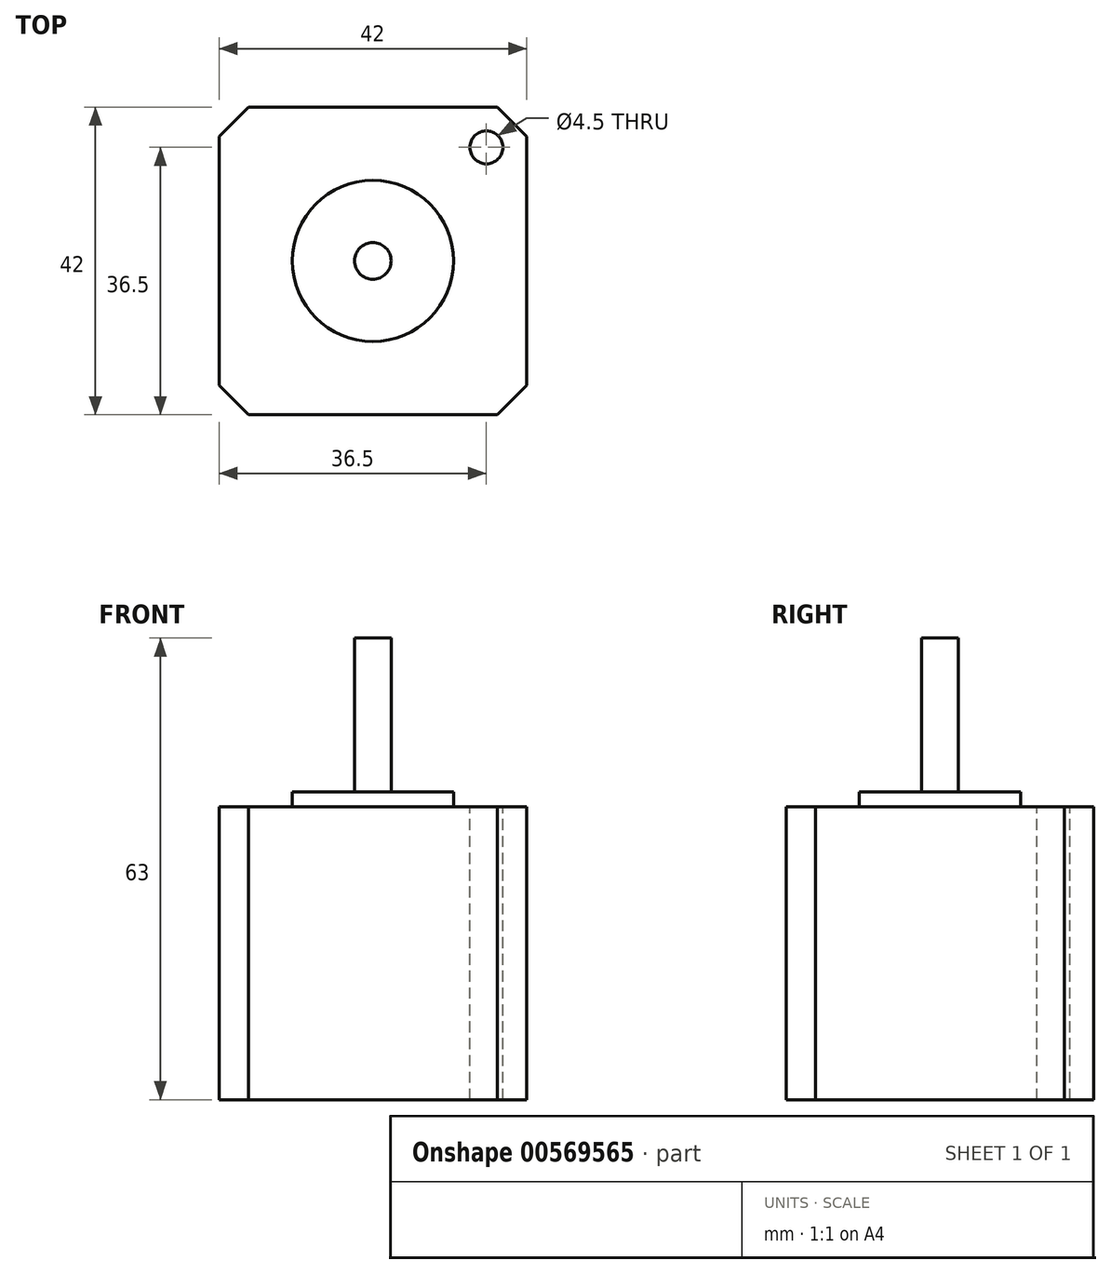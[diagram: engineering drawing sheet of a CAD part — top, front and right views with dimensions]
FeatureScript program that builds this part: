
annotation { "Feature Type Name" : "Feature", "Feature Type Description" : "" }
export const myFeature = defineFeature(function(context is Context, id is Id, definition is map)
    precondition{}
    {
        {
            var Q0;
            Q0=qCreatedBy(makeId("Front.planeOp"),FACE);
            var sketch = newSketch(context, id + "F0", { "sketchPlane" : qUnion([Q0])});
            skLineSegment(sketch, "E0", {"start": v(0, 0) * mm, "end": v(0, 73.77) * mm});
            skSolve(sketch);
        }
        {
            var Q0;
            Q0=qCreatedBy(makeId("Top.planeOp"),FACE);
            var sketch = newSketch(context, id + "F1", { "sketchPlane" : qUnion([Q0])});
            skLineSegment(sketch, "E1.bottom", {"start": v(21, 21) * mm, "end": v(-21, 21) * mm});
            skLineSegment(sketch, "E1.top", {"start": v(21, -21) * mm, "end": v(-21, -21) * mm});
            skLineSegment(sketch, "E1.left", {"start": v(21, 21) * mm, "end": v(21, -21) * mm});
            skLineSegment(sketch, "E1.right", {"start": v(-21, 21) * mm, "end": v(-21, -21) * mm});
            skPoint(sketch, "E1.middle", {"position": v(0, 0) * mm});
            skSolve(sketch);
        }
        {
            var Q0;
            Q0=makeQuery(id+"F1.imprint","IMPRINT",FACE,{"disambiguationData":[TD([[makeQuery(id+"F1.imprint","IMPRINT",EDGE,{"derivedFrom":sQuery(id+"F1.wireOp",EDGE,"E1.bottom")}),1.0]])]});
            extrude(context, id + "F2", {"entities" : qUnion([Q0]), "depth" : 40 * mm, "offsetDistance" : 25 * mm});
        }
        {
            var Q0;
            Q0=makeQuery(id+"F2.opExtrude","CAP_FACE",FACE,{"disambiguationData":[OSD([sQuery(id+"F1.wireOp",EDGE,"E1.bottom"),sQuery(id+"F1.wireOp",EDGE,"E1.top"),sQuery(id+"F1.wireOp",EDGE,"E1.left"),sQuery(id+"F1.wireOp",EDGE,"E1.right")])],"isStart":false});
            var sketch = newSketch(context, id + "F3", { "sketchPlane" : qUnion([Q0])});
            skCircle(sketch, "E2", {"center": v(0, 0) * mm, "radius": 11 * mm});
            skSolve(sketch);
        }
        {
            var Q0;
            Q0 = qSketchRegion(id + "F3", true);
            extrude(context, id + "F4", {"entities" : qUnion([Q0]), "operationType" : NewBodyOperationType.ADD, "depth" : 2 * mm, "offsetDistance" : 25 * mm});
        }
        {
            var Q0;
            Q0=makeQuery(id+"F4.opExtrude","CAP_FACE",FACE,{"disambiguationData":[OSD([sQuery(id+"F3.wireOp",EDGE,"E2")])],"isStart":false});
            var sketch = newSketch(context, id + "F5", { "sketchPlane" : qUnion([Q0])});
            skCircle(sketch, "E3", {"center": v(0, 0) * mm, "radius": 2.5 * mm});
            skSolve(sketch);
        }
        {
            var Q0;
            Q0 = qSketchRegion(id + "F5", true);
            extrude(context, id + "F6", {"entities" : qUnion([Q0]), "operationType" : NewBodyOperationType.ADD, "depth" : 21 * mm, "offsetDistance" : 25 * mm});
        }
        {
            var Q0;
            Q0=makeQuery(id+"F2.opExtrude","CAP_FACE",FACE,{"disambiguationData":[OSD([sQuery(id+"F1.wireOp",EDGE,"E1.bottom"),sQuery(id+"F1.wireOp",EDGE,"E1.top"),sQuery(id+"F1.wireOp",EDGE,"E1.left"),sQuery(id+"F1.wireOp",EDGE,"E1.right")])],"isStart":false});
            var sketch = newSketch(context, id + "F7", { "sketchPlane" : qUnion([Q0])});
            skPoint(sketch, "E4", {"position": v(15.5, 15.5) * mm});
            skSolve(sketch);
        }
        {
            var Q0;
            Q0=sQuery(id+"F7.wireOp",VERTEX,"E4");
            var Q1;
            Q1=makeQuery(id+"F2.opExtrude","SWEPT_BODY",BODY,{"disambiguationData":[OSD([sQuery(id+"F1.wireOp",EDGE,"E1.bottom"),sQuery(id+"F1.wireOp",EDGE,"E1.top"),sQuery(id+"F1.wireOp",EDGE,"E1.left"),sQuery(id+"F1.wireOp",EDGE,"E1.right")])]});
            hole(context, id + "F8", {"style" : HoleStyle.SIMPLE, "endStyle" : HoleEndStyle.THROUGH, "holeDiameter" : 4.5 * mm, "isTappedThrough" : true, "tappedDepth" : 12 * mm, "tapClearance" : 3, "locations" : qUnion([Q0]), "scope" : qUnion([Q1])});
        }
        {
            var Q0;
            Q0=makeQuery(id+"F2.opExtrude","SWEPT_EDGE",EDGE,{"disambiguationData":[OSD([sQuery(id+"F1.wireOp",EDGE,"E1.bottom"),sQuery(id+"F1.wireOp",EDGE,"E1.left")])]});
            var Q1;
            Q1=makeQuery(id+"F2.opExtrude","SWEPT_EDGE",EDGE,{"disambiguationData":[OSD([sQuery(id+"F1.wireOp",EDGE,"E1.top"),sQuery(id+"F1.wireOp",EDGE,"E1.left")])]});
            var Q2;
            Q2=makeQuery(id+"F2.opExtrude","SWEPT_EDGE",EDGE,{"disambiguationData":[OSD([sQuery(id+"F1.wireOp",EDGE,"E1.top"),sQuery(id+"F1.wireOp",EDGE,"E1.right")])]});
            var Q3;
            Q3=makeQuery(id+"F2.opExtrude","SWEPT_EDGE",EDGE,{"disambiguationData":[OSD([sQuery(id+"F1.wireOp",EDGE,"E1.bottom"),sQuery(id+"F1.wireOp",EDGE,"E1.right")])]});
            chamfer(context, id + "F9", {"entities" : qUnion([Q0, Q1, Q2, Q3]), "width" : 4 * mm, "tangentPropagation" : true});
        }
    });
